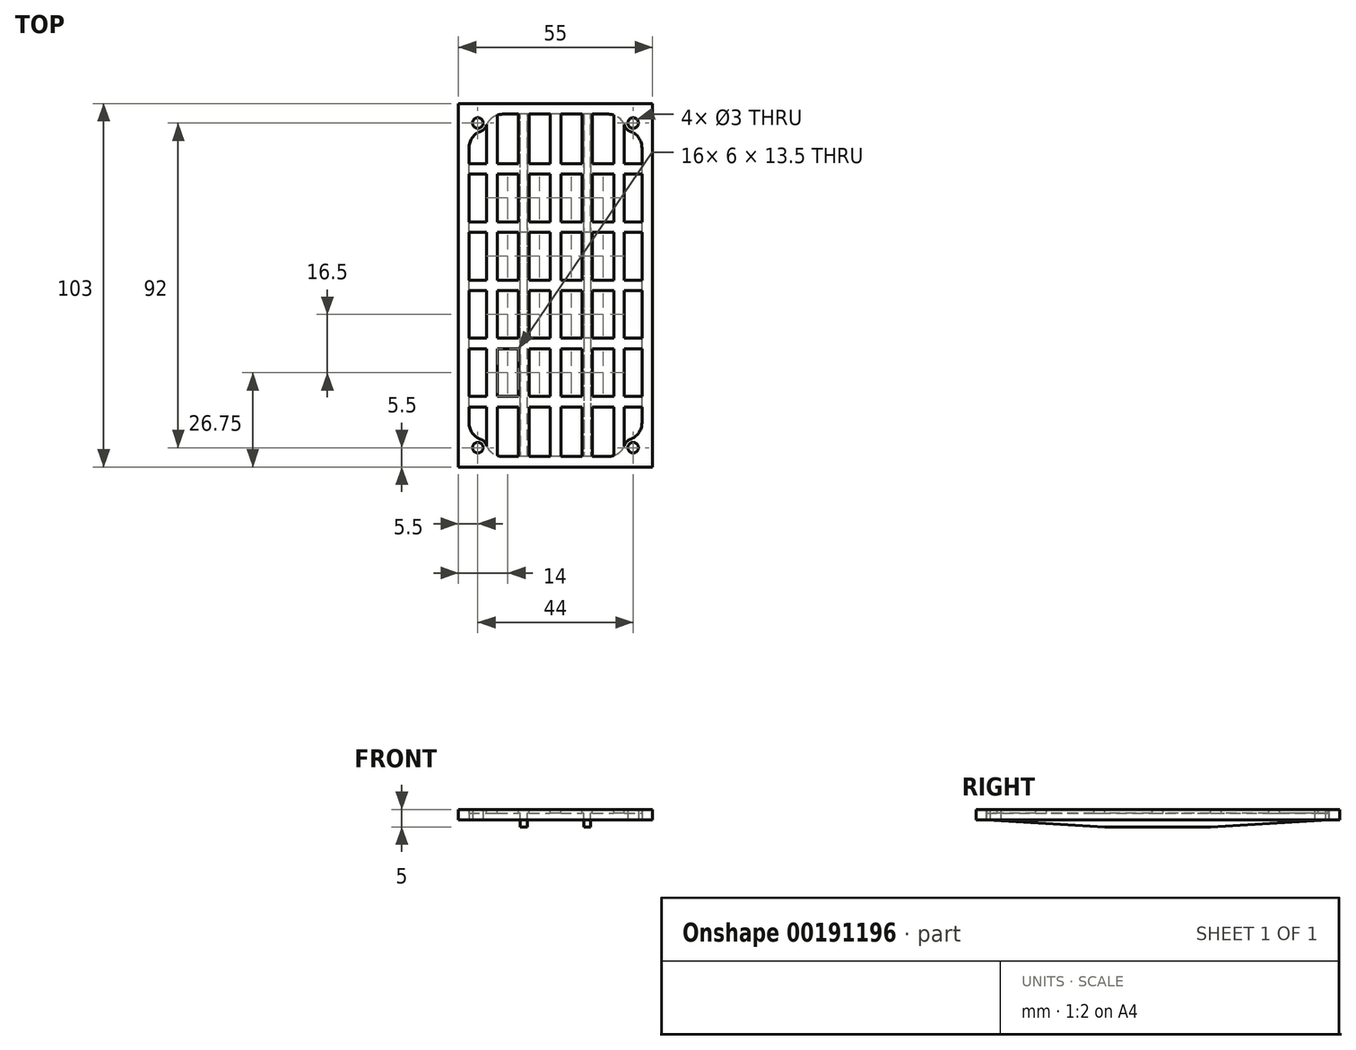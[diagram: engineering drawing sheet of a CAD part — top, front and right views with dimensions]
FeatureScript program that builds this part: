
annotation { "Feature Type Name" : "Feature", "Feature Type Description" : "" }
export const myFeature = defineFeature(function(context is Context, id is Id, definition is map)
    precondition{}
    {
        {
            var Q0;
            Q0=qCreatedBy(makeId("Top.planeOp"),FACE);
            var sketch = newSketch(context, id + "F0", { "sketchPlane" : qUnion([Q0])});
            skLineSegment(sketch, "E0.bottom", {"start": v(27.5, -51.5) * mm, "end": v(-27.5, -51.5) * mm});
            skLineSegment(sketch, "E0.top", {"start": v(27.5, 51.5) * mm, "end": v(-27.5, 51.5) * mm});
            skLineSegment(sketch, "E0.left", {"start": v(27.5, -51.5) * mm, "end": v(27.5, 51.5) * mm});
            skLineSegment(sketch, "E0.right", {"start": v(-27.5, -51.5) * mm, "end": v(-27.5, 51.5) * mm});
            skLineSegment(sketch, "E1.0", {"start": v(-27.5, -51.5) * mm, "end": v(-27.5, 48.5) * mm});
            skLineSegment(sketch, "E2.0", {"start": v(14.93, 48.5) * mm, "end": v(-14.93, 48.5) * mm});
            skLineSegment(sketch, "E3.0", {"start": v(14.93, -48.5) * mm, "end": v(-14.93, -48.5) * mm});
            skLineSegment(sketch, "E4.0", {"start": v(24.5, -38.93) * mm, "end": v(24.5, 38.93) * mm});
            skCircle(sketch, "E5", {"center": v(-22, 46) * mm, "radius": 1.5 * mm});
            skArc(sketch, "E6", {"start": v(-21.17, 43.64) * mm, "mid": v(-20.23, 44.23) * mm, "end": v(-19.64, 45.17) * mm});
            skCircle(sketch, "E7", {"center": v(22, 46) * mm, "radius": 1.5 * mm});
            skArc(sketch, "E8", {"start": v(19.64, 45.17) * mm, "mid": v(20.23, 44.23) * mm, "end": v(21.17, 43.64) * mm});
            skCircle(sketch, "E9", {"center": v(-22, -46) * mm, "radius": 1.5 * mm});
            skArc(sketch, "E10", {"start": v(-19.64, -45.17) * mm, "mid": v(-20.23, -44.23) * mm, "end": v(-21.17, -43.64) * mm});
            skCircle(sketch, "E11", {"center": v(22, -46) * mm, "radius": 1.5 * mm});
            skArc(sketch, "E12", {"start": v(21.17, -43.64) * mm, "mid": v(20.23, -44.23) * mm, "end": v(19.64, -45.17) * mm});
            skPoint(sketch, "E13.visualSharp", {"position": v(24.5, -46) * mm});
            skArc(sketch, "E13.filletArc", {"start": v(21.17, -43.64) * mm, "mid": v(23.58, -41.82) * mm, "end": v(24.5, -38.93) * mm});
            skPoint(sketch, "E14.visualSharp", {"position": v(22, -48.5) * mm});
            skArc(sketch, "E14.filletArc", {"start": v(14.93, -48.5) * mm, "mid": v(17.82, -47.58) * mm, "end": v(19.64, -45.17) * mm});
            skPoint(sketch, "E15.visualSharp", {"position": v(22, 48.5) * mm});
            skArc(sketch, "E15.filletArc", {"start": v(19.64, 45.17) * mm, "mid": v(17.82, 47.58) * mm, "end": v(14.93, 48.5) * mm});
            skPoint(sketch, "E16.visualSharp", {"position": v(24.5, 46) * mm});
            skArc(sketch, "E16.filletArc", {"start": v(24.5, 38.93) * mm, "mid": v(23.58, 41.82) * mm, "end": v(21.17, 43.64) * mm});
            skLineSegment(sketch, "E17", {"start": v(-24.5, -38.93) * mm, "end": v(-24.5, 38.93) * mm});
            skPoint(sketch, "E18.visualSharp", {"position": v(-24.5, -46) * mm});
            skArc(sketch, "E18.filletArc", {"start": v(-24.5, -38.93) * mm, "mid": v(-23.58, -41.82) * mm, "end": v(-21.17, -43.64) * mm});
            skPoint(sketch, "E19.visualSharp", {"position": v(-22, -48.5) * mm});
            skArc(sketch, "E19.filletArc", {"start": v(-19.64, -45.17) * mm, "mid": v(-17.82, -47.58) * mm, "end": v(-14.93, -48.5) * mm});
            skPoint(sketch, "E20.visualSharp", {"position": v(-24.5, 46) * mm});
            skArc(sketch, "E20.filletArc", {"start": v(-21.17, 43.64) * mm, "mid": v(-23.58, 41.82) * mm, "end": v(-24.5, 38.93) * mm});
            skPoint(sketch, "E21.visualSharp", {"position": v(-22, 48.5) * mm});
            skArc(sketch, "E21.filletArc", {"start": v(-14.93, 48.5) * mm, "mid": v(-17.82, 47.58) * mm, "end": v(-19.64, 45.17) * mm});
            skSolve(sketch);
        }
        {
            var Q0;
            Q0 = qSketchRegion(id + "F0", true);
            extrude(context, id + "F1", {"entities" : qUnion([Q0]), "depth" : 3 * mm});
        }
        {
            var Q0;
            Q0=makeQuery(id+"F1.opExtrude","CAP_FACE",FACE,{"disambiguationData":[OSD([sQuery(id+"F0.wireOp",EDGE,"E0.bottom"),sQuery(id+"F0.wireOp",EDGE,"E0.top"),sQuery(id+"F0.wireOp",EDGE,"E0.left"),sQuery(id+"F0.wireOp",EDGE,"E0.right"),sQuery(id+"F0.wireOp",EDGE,"E2.0"),sQuery(id+"F0.wireOp",EDGE,"E3.0"),sQuery(id+"F0.wireOp",EDGE,"E4.0"),sQuery(id+"F0.wireOp",EDGE,"E5"),sQuery(id+"F0.wireOp",EDGE,"E6"),sQuery(id+"F0.wireOp",EDGE,"E7"),sQuery(id+"F0.wireOp",EDGE,"E8"),sQuery(id+"F0.wireOp",EDGE,"E9"),sQuery(id+"F0.wireOp",EDGE,"E10"),sQuery(id+"F0.wireOp",EDGE,"E11"),sQuery(id+"F0.wireOp",EDGE,"E12"),sQuery(id+"F0.wireOp",EDGE,"E13.filletArc"),sQuery(id+"F0.wireOp",EDGE,"E14.filletArc"),sQuery(id+"F0.wireOp",EDGE,"E15.filletArc"),sQuery(id+"F0.wireOp",EDGE,"E16.filletArc"),sQuery(id+"F0.wireOp",EDGE,"E17"),sQuery(id+"F0.wireOp",EDGE,"E18.filletArc"),sQuery(id+"F0.wireOp",EDGE,"E19.filletArc"),sQuery(id+"F0.wireOp",EDGE,"E20.filletArc"),sQuery(id+"F0.wireOp",EDGE,"E21.filletArc")])],"isStart":false});
            var sketch = newSketch(context, id + "F2", { "sketchPlane" : qUnion([Q0])});
            skLineSegment(sketch, "E22.0", {"start": v(14.93, 48.5) * mm, "end": v(-14.93, 48.5) * mm});
            skLineSegment(sketch, "E22.1", {"start": v(14.93, -48.5) * mm, "end": v(-14.93, -48.5) * mm});
            skLineSegment(sketch, "E22.2", {"start": v(24.5, -38.93) * mm, "end": v(24.5, 38.93) * mm});
            skLineSegment(sketch, "E22.3", {"start": v(-24.5, -38.93) * mm, "end": v(-24.5, 38.93) * mm});
            skArc(sketch, "E22.4", {"start": v(-19.64, -45.17) * mm, "mid": v(-17.82, -47.58) * mm, "end": v(-14.93, -48.5) * mm});
            skArc(sketch, "E22.5", {"start": v(-24.5, -38.93) * mm, "mid": v(-23.58, -41.82) * mm, "end": v(-21.17, -43.64) * mm});
            skArc(sketch, "E22.6", {"start": v(-19.64, -45.17) * mm, "mid": v(-20.23, -44.23) * mm, "end": v(-21.17, -43.64) * mm});
            skArc(sketch, "E22.7", {"start": v(14.93, -48.5) * mm, "mid": v(17.82, -47.58) * mm, "end": v(19.64, -45.17) * mm});
            skArc(sketch, "E22.8", {"start": v(21.17, -43.64) * mm, "mid": v(23.58, -41.82) * mm, "end": v(24.5, -38.93) * mm});
            skArc(sketch, "E22.9", {"start": v(21.17, -43.64) * mm, "mid": v(20.23, -44.23) * mm, "end": v(19.64, -45.17) * mm});
            skArc(sketch, "E22.10", {"start": v(24.5, 38.93) * mm, "mid": v(23.58, 41.82) * mm, "end": v(21.17, 43.64) * mm});
            skArc(sketch, "E22.11", {"start": v(19.64, 45.17) * mm, "mid": v(20.23, 44.23) * mm, "end": v(21.17, 43.64) * mm});
            skArc(sketch, "E22.12", {"start": v(19.64, 45.17) * mm, "mid": v(17.82, 47.58) * mm, "end": v(14.93, 48.5) * mm});
            skArc(sketch, "E22.13", {"start": v(-21.17, 43.64) * mm, "mid": v(-23.58, 41.82) * mm, "end": v(-24.5, 38.93) * mm});
            skArc(sketch, "E22.14", {"start": v(-14.93, 48.5) * mm, "mid": v(-17.82, 47.58) * mm, "end": v(-19.64, 45.17) * mm});
            skArc(sketch, "E22.15", {"start": v(-21.17, 43.64) * mm, "mid": v(-20.23, 44.23) * mm, "end": v(-19.64, 45.17) * mm});
            skPoint(sketch, "E22.16", {"position": v(17.82, -47.58) * mm});
            skPoint(sketch, "E22.17", {"position": v(20.23, -44.23) * mm});
            skLineSegment(sketch, "E23.0", {"start": v(-1.5, 48.5) * mm, "end": v(-1.5, 34.5) * mm});
            skLineSegment(sketch, "E24.0", {"start": v(1.5, 48.5) * mm, "end": v(1.5, 34.5) * mm});
            skLineSegment(sketch, "E25.1.0.0", {"start": v(10.5, 48.5) * mm, "end": v(10.5, 34.5) * mm});
            skLineSegment(sketch, "E25.1.0.1", {"start": v(7.5, 48.5) * mm, "end": v(7.5, 34.5) * mm});
            skLineSegment(sketch, "E25.2.0.0", {"start": v(19.5, 45.53) * mm, "end": v(19.5, 34.5) * mm});
            skLineSegment(sketch, "E25.2.0.1", {"start": v(16.5, 48.25) * mm, "end": v(16.5, 34.5) * mm});
            skLineSegment(sketch, "E25.direction1", {"start": v(-1.5, -48.5) * mm, "end": v(7.5, -48.5) * mm, "construction": true});
            skLineSegment(sketch, "E26.MirrorCS", {"start": v(-7.5, 48.5) * mm, "end": v(-7.5, 34.5) * mm});
            skLineSegment(sketch, "E27.MirrorCS", {"start": v(-10.5, 48.5) * mm, "end": v(-10.5, 34.5) * mm});
            skLineSegment(sketch, "E28.MirrorCS", {"start": v(-19.5, 45.53) * mm, "end": v(-19.5, 34.5) * mm});
            skLineSegment(sketch, "E29.MirrorCS", {"start": v(-16.5, 48.25) * mm, "end": v(-16.5, 34.5) * mm});
            skLineSegment(sketch, "E30.0", {"start": v(-24.5, -1.5) * mm, "end": v(-19.5, -1.5) * mm});
            skLineSegment(sketch, "E31.0", {"start": v(-24.5, 1.5) * mm, "end": v(-19.5, 1.5) * mm});
            skLineSegment(sketch, "E32.0.1.0", {"start": v(-24.5, 18) * mm, "end": v(-19.5, 18) * mm});
            skLineSegment(sketch, "E32.0.1.1", {"start": v(-24.5, 15) * mm, "end": v(-19.5, 15) * mm});
            skLineSegment(sketch, "E32.direction1", {"start": v(-24.5, -1.5) * mm, "end": v(-19.5, -1.5) * mm, "construction": true});
            skLineSegment(sketch, "E32.direction2", {"start": v(-24.5, -1.5) * mm, "end": v(-24.5, 15) * mm, "construction": true});
            skLineSegment(sketch, "E33.0.0.2", {"start": v(-24.5, 34.5) * mm, "end": v(-19.5, 34.5) * mm});
            skLineSegment(sketch, "E33.3.0.2", {"start": v(-24.5, 31.5) * mm, "end": v(-19.5, 31.5) * mm});
            skLineSegment(sketch, "E34.MirrorCS", {"start": v(-24.5, -18) * mm, "end": v(-19.5, -18) * mm});
            skLineSegment(sketch, "E35.MirrorCS", {"start": v(-24.5, -31.5) * mm, "end": v(-19.5, -31.5) * mm});
            skLineSegment(sketch, "E36.MirrorCS", {"start": v(-24.5, -15) * mm, "end": v(-19.5, -15) * mm});
            skLineSegment(sketch, "E37.MirrorCS", {"start": v(-24.5, -34.5) * mm, "end": v(-19.5, -34.5) * mm});
            skPoint(sketch, "E38.orphan", {"position": v(-19.5, 48.5) * mm});
            skPoint(sketch, "E39.orphan", {"position": v(-16.5, 48.5) * mm});
            skLineSegment(sketch, "E40.trimOffspring", {"start": v(-16.5, 34.5) * mm, "end": v(-10.5, 34.5) * mm});
            skLineSegment(sketch, "E41.trimOffspring", {"start": v(-16.5, 31.5) * mm, "end": v(-10.5, 31.5) * mm});
            skLineSegment(sketch, "E42.trimOffspring", {"start": v(-16.5, 31.5) * mm, "end": v(-16.5, 18) * mm});
            skLineSegment(sketch, "E43.trimOffspring", {"start": v(-19.5, 31.5) * mm, "end": v(-19.5, 18) * mm});
            skLineSegment(sketch, "E44.trimOffspring", {"start": v(-10.5, 31.5) * mm, "end": v(-10.5, 18) * mm});
            skLineSegment(sketch, "E45.trimOffspring", {"start": v(-7.5, 31.5) * mm, "end": v(-7.5, 18) * mm});
            skLineSegment(sketch, "E46.trimOffspring", {"start": v(-7.5, 34.5) * mm, "end": v(-1.5, 34.5) * mm});
            skLineSegment(sketch, "E47.trimOffspring", {"start": v(-7.5, 31.5) * mm, "end": v(-1.5, 31.5) * mm});
            skLineSegment(sketch, "E48.trimOffspring", {"start": v(1.5, 31.5) * mm, "end": v(7.5, 31.5) * mm});
            skLineSegment(sketch, "E49.trimOffspring", {"start": v(1.5, 34.5) * mm, "end": v(7.5, 34.5) * mm});
            skLineSegment(sketch, "E50.trimOffspring", {"start": v(1.5, 31.5) * mm, "end": v(1.5, 18) * mm});
            skLineSegment(sketch, "E51.trimOffspring", {"start": v(-1.5, 31.5) * mm, "end": v(-1.5, 18) * mm});
            skLineSegment(sketch, "E52.trimOffspring", {"start": v(7.5, 31.5) * mm, "end": v(7.5, 18) * mm});
            skLineSegment(sketch, "E53.trimOffspring", {"start": v(10.5, 31.5) * mm, "end": v(10.5, 18) * mm});
            skLineSegment(sketch, "E54.trimOffspring", {"start": v(10.5, 34.5) * mm, "end": v(16.5, 34.5) * mm});
            skLineSegment(sketch, "E55.trimOffspring", {"start": v(10.5, 31.5) * mm, "end": v(16.5, 31.5) * mm});
            skLineSegment(sketch, "E56.trimOffspring", {"start": v(19.5, 34.5) * mm, "end": v(24.5, 34.5) * mm});
            skLineSegment(sketch, "E57.trimOffspring", {"start": v(19.5, 31.5) * mm, "end": v(24.5, 31.5) * mm});
            skLineSegment(sketch, "E58.trimOffspring", {"start": v(19.5, 31.5) * mm, "end": v(19.5, 18) * mm});
            skLineSegment(sketch, "E59.trimOffspring", {"start": v(16.5, 31.5) * mm, "end": v(16.5, 18) * mm});
            skPoint(sketch, "E60.orphan", {"position": v(19.5, 48.5) * mm});
            skPoint(sketch, "E61.orphan", {"position": v(16.5, 48.5) * mm});
            skLineSegment(sketch, "E62.trimOffspring", {"start": v(-16.5, 18) * mm, "end": v(-10.5, 18) * mm});
            skLineSegment(sketch, "E63.trimOffspring", {"start": v(-7.5, 18) * mm, "end": v(-1.5, 18) * mm});
            skLineSegment(sketch, "E64.trimOffspring", {"start": v(1.5, 18) * mm, "end": v(7.5, 18) * mm});
            skLineSegment(sketch, "E65.trimOffspring", {"start": v(10.5, 18) * mm, "end": v(16.5, 18) * mm});
            skLineSegment(sketch, "E66.trimOffspring", {"start": v(19.5, 18) * mm, "end": v(24.5, 18) * mm});
            skLineSegment(sketch, "E67.trimOffspring", {"start": v(19.5, 15) * mm, "end": v(24.5, 15) * mm});
            skLineSegment(sketch, "E68.trimOffspring", {"start": v(19.5, 15) * mm, "end": v(19.5, 1.5) * mm});
            skLineSegment(sketch, "E69.trimOffspring", {"start": v(16.5, 15) * mm, "end": v(16.5, 1.5) * mm});
            skLineSegment(sketch, "E70.trimOffspring", {"start": v(10.5, 15) * mm, "end": v(10.5, 1.5) * mm});
            skLineSegment(sketch, "E71.trimOffspring", {"start": v(7.5, 15) * mm, "end": v(7.5, 1.5) * mm});
            skLineSegment(sketch, "E72.trimOffspring", {"start": v(1.5, 15) * mm, "end": v(1.5, 1.5) * mm});
            skLineSegment(sketch, "E73.trimOffspring", {"start": v(-1.5, 15) * mm, "end": v(-1.5, 1.5) * mm});
            skLineSegment(sketch, "E74.trimOffspring", {"start": v(-7.5, 15) * mm, "end": v(-7.5, 1.5) * mm});
            skLineSegment(sketch, "E75.trimOffspring", {"start": v(-10.5, 15) * mm, "end": v(-10.5, 1.5) * mm});
            skLineSegment(sketch, "E76.trimOffspring", {"start": v(-16.5, 15) * mm, "end": v(-16.5, 1.5) * mm});
            skLineSegment(sketch, "E77.trimOffspring", {"start": v(-19.5, 15) * mm, "end": v(-19.5, 1.5) * mm});
            skLineSegment(sketch, "E78.trimOffspring", {"start": v(-16.5, 15) * mm, "end": v(-10.5, 15) * mm});
            skLineSegment(sketch, "E79.trimOffspring", {"start": v(-7.5, 15) * mm, "end": v(-1.5, 15) * mm});
            skLineSegment(sketch, "E80.trimOffspring", {"start": v(1.5, 15) * mm, "end": v(7.5, 15) * mm});
            skLineSegment(sketch, "E81.trimOffspring", {"start": v(10.5, 15) * mm, "end": v(16.5, 15) * mm});
            skLineSegment(sketch, "E82.trimOffspring", {"start": v(-16.5, 1.5) * mm, "end": v(-10.5, 1.5) * mm});
            skLineSegment(sketch, "E83.trimOffspring", {"start": v(-16.5, -1.5) * mm, "end": v(-10.5, -1.5) * mm, "construction": true});
            skLineSegment(sketch, "E84.trimOffspring", {"start": v(-16.5, -1.5) * mm, "end": v(-16.5, -15) * mm});
            skLineSegment(sketch, "E85.trimOffspring", {"start": v(19.5, 1.5) * mm, "end": v(24.5, 1.5) * mm});
            skLineSegment(sketch, "E86.trimOffspring", {"start": v(19.5, -1.5) * mm, "end": v(24.5, -1.5) * mm});
            skLineSegment(sketch, "E87.trimOffspring", {"start": v(19.5, -1.5) * mm, "end": v(19.5, -15) * mm});
            skLineSegment(sketch, "E88.trimOffspring", {"start": v(16.5, -1.5) * mm, "end": v(16.5, -15) * mm});
            skLineSegment(sketch, "E89.trimOffspring", {"start": v(10.5, -1.5) * mm, "end": v(10.5, -15) * mm});
            skLineSegment(sketch, "E90.trimOffspring", {"start": v(7.5, -1.5) * mm, "end": v(7.5, -15) * mm});
            skLineSegment(sketch, "E91.trimOffspring", {"start": v(1.5, -1.5) * mm, "end": v(1.5, -15) * mm});
            skLineSegment(sketch, "E92.trimOffspring", {"start": v(-1.5, -1.5) * mm, "end": v(-1.5, -15) * mm});
            skLineSegment(sketch, "E93.trimOffspring", {"start": v(1.5, 1.5) * mm, "end": v(7.5, 1.5) * mm});
            skLineSegment(sketch, "E94.trimOffspring", {"start": v(10.5, -1.5) * mm, "end": v(16.5, -1.5) * mm});
            skLineSegment(sketch, "E95.trimOffspring", {"start": v(10.5, 1.5) * mm, "end": v(16.5, 1.5) * mm});
            skLineSegment(sketch, "E96.trimOffspring", {"start": v(1.5, -1.5) * mm, "end": v(7.5, -1.5) * mm});
            skLineSegment(sketch, "E97.trimOffspring", {"start": v(-7.5, -1.5) * mm, "end": v(-1.5, -1.5) * mm, "construction": true});
            skLineSegment(sketch, "E98.trimOffspring", {"start": v(-7.5, 1.5) * mm, "end": v(-1.5, 1.5) * mm});
            skLineSegment(sketch, "E99.trimOffspring", {"start": v(-7.5, -1.5) * mm, "end": v(-7.5, -15) * mm});
            skLineSegment(sketch, "E100.trimOffspring", {"start": v(-10.5, -1.5) * mm, "end": v(-10.5, -15) * mm});
            skLineSegment(sketch, "E101.trimOffspring", {"start": v(-19.5, -1.5) * mm, "end": v(-19.5, -15) * mm});
            skLineSegment(sketch, "E102.trimOffspring", {"start": v(-16.5, -1.5) * mm, "end": v(-10.5, -1.5) * mm});
            skLineSegment(sketch, "E103.trimOffspring", {"start": v(-7.5, -1.5) * mm, "end": v(-1.5, -1.5) * mm});
            skLineSegment(sketch, "E104.trimOffspring", {"start": v(-16.5, -15) * mm, "end": v(-10.5, -15) * mm});
            skLineSegment(sketch, "E105.trimOffspring", {"start": v(-16.5, -18) * mm, "end": v(-10.5, -18) * mm});
            skLineSegment(sketch, "E106.trimOffspring", {"start": v(-16.5, -18) * mm, "end": v(-16.5, -31.5) * mm});
            skLineSegment(sketch, "E107.trimOffspring", {"start": v(-19.5, -18) * mm, "end": v(-19.5, -31.5) * mm});
            skLineSegment(sketch, "E108.trimOffspring", {"start": v(-10.5, -18) * mm, "end": v(-10.5, -31.5) * mm});
            skLineSegment(sketch, "E109.trimOffspring", {"start": v(-7.5, -18) * mm, "end": v(-7.5, -31.5) * mm});
            skLineSegment(sketch, "E110.trimOffspring", {"start": v(-7.5, -15) * mm, "end": v(-1.5, -15) * mm});
            skLineSegment(sketch, "E111.trimOffspring", {"start": v(-7.5, -18) * mm, "end": v(-1.5, -18) * mm});
            skLineSegment(sketch, "E112.trimOffspring", {"start": v(1.5, -18) * mm, "end": v(7.5, -18) * mm});
            skLineSegment(sketch, "E113.trimOffspring", {"start": v(1.5, -18) * mm, "end": v(1.5, -31.5) * mm});
            skLineSegment(sketch, "E114.trimOffspring", {"start": v(-1.5, -18) * mm, "end": v(-1.5, -31.5) * mm});
            skLineSegment(sketch, "E115.trimOffspring", {"start": v(7.5, -18) * mm, "end": v(7.5, -31.5) * mm});
            skLineSegment(sketch, "E116.trimOffspring", {"start": v(10.5, -18) * mm, "end": v(10.5, -31.5) * mm});
            skLineSegment(sketch, "E117.trimOffspring", {"start": v(10.5, -15) * mm, "end": v(16.5, -15) * mm});
            skLineSegment(sketch, "E118.trimOffspring", {"start": v(10.5, -18) * mm, "end": v(16.5, -18) * mm});
            skLineSegment(sketch, "E119.trimOffspring", {"start": v(1.5, -15) * mm, "end": v(7.5, -15) * mm});
            skLineSegment(sketch, "E120.trimOffspring", {"start": v(19.5, -15) * mm, "end": v(24.5, -15) * mm});
            skLineSegment(sketch, "E121.trimOffspring", {"start": v(19.5, -18) * mm, "end": v(24.5, -18) * mm});
            skLineSegment(sketch, "E122.trimOffspring", {"start": v(19.5, -18) * mm, "end": v(19.5, -31.5) * mm});
            skLineSegment(sketch, "E123.trimOffspring", {"start": v(16.5, -18) * mm, "end": v(16.5, -31.5) * mm});
            skLineSegment(sketch, "E124.trimOffspring", {"start": v(-16.5, -31.5) * mm, "end": v(-10.5, -31.5) * mm});
            skLineSegment(sketch, "E125.trimOffspring", {"start": v(-16.5, -34.5) * mm, "end": v(-10.5, -34.5) * mm});
            skLineSegment(sketch, "E126.trimOffspring", {"start": v(-16.5, -34.5) * mm, "end": v(-16.5, -48.25) * mm});
            skLineSegment(sketch, "E127.trimOffspring", {"start": v(-19.5, -34.5) * mm, "end": v(-19.5, -45.53) * mm});
            skLineSegment(sketch, "E128.trimOffspring", {"start": v(-10.5, -34.5) * mm, "end": v(-10.5, -48.5) * mm});
            skLineSegment(sketch, "E129.trimOffspring", {"start": v(-7.5, -34.5) * mm, "end": v(-7.5, -48.5) * mm});
            skLineSegment(sketch, "E130.trimOffspring", {"start": v(1.5, -34.5) * mm, "end": v(7.5, -34.5) * mm});
            skLineSegment(sketch, "E131.trimOffspring", {"start": v(1.5, -31.5) * mm, "end": v(7.5, -31.5) * mm});
            skLineSegment(sketch, "E132.trimOffspring", {"start": v(10.5, -34.5) * mm, "end": v(16.5, -34.5) * mm});
            skLineSegment(sketch, "E133.trimOffspring", {"start": v(19.5, -31.5) * mm, "end": v(24.5, -31.5) * mm});
            skLineSegment(sketch, "E134.trimOffspring", {"start": v(19.5, -34.5) * mm, "end": v(24.5, -34.5) * mm});
            skLineSegment(sketch, "E135.trimOffspring", {"start": v(19.5, -34.5) * mm, "end": v(19.5, -45.53) * mm});
            skLineSegment(sketch, "E136.trimOffspring", {"start": v(16.5, -34.5) * mm, "end": v(16.5, -48.25) * mm});
            skLineSegment(sketch, "E137.trimOffspring", {"start": v(10.5, -34.5) * mm, "end": v(10.5, -48.5) * mm});
            skLineSegment(sketch, "E138.trimOffspring", {"start": v(10.5, -31.5) * mm, "end": v(16.5, -31.5) * mm});
            skLineSegment(sketch, "E139.trimOffspring", {"start": v(7.5, -34.5) * mm, "end": v(7.5, -48.5) * mm});
            skLineSegment(sketch, "E140.trimOffspring", {"start": v(1.5, -34.5) * mm, "end": v(1.5, -48.5) * mm});
            skLineSegment(sketch, "E141", {"start": v(-7.5, -31.5) * mm, "end": v(-1.5, -31.5) * mm});
            skLineSegment(sketch, "E142", {"start": v(-7.5, -34.5) * mm, "end": v(-1.5, -34.5) * mm});
            skLineSegment(sketch, "E143.trimOffspring", {"start": v(-1.5, -34.5) * mm, "end": v(-1.5, -48.5) * mm});
            skPoint(sketch, "E144.orphan", {"position": v(19.5, -48.5) * mm});
            skPoint(sketch, "E145.orphan", {"position": v(16.5, -48.5) * mm});
            skPoint(sketch, "E146.orphan", {"position": v(-16.5, -48.5) * mm});
            skPoint(sketch, "E147.orphan", {"position": v(-19.5, -48.5) * mm});
            skSolve(sketch);
        }
        {
            var Q0;
            {var subQ19=sQuery(id+"F2.wireOp",EDGE,"E23.0");Q0=makeQuery(id+"F2.imprint","IMPRINT",FACE,{"disambiguationData":[TD([[makeQuery(id+"F2.imprint","IMPRINT",EDGE,{"derivedFrom":subQ19}),1.0]])]});}
            extrude(context, id + "F3", {"entities" : qUnion([Q0]), "operationType" : NewBodyOperationType.ADD, "oppositeDirection" : true, "depth" : 1 * mm});
        }
        {
            var Q0;
            Q0=makeQuery(id+"F3.opExtrude","CAP_FACE",FACE,{"disambiguationData":[OSD([sQuery(id+"F2.wireOp",EDGE,"E22.0"),sQuery(id+"F2.wireOp",EDGE,"E22.1"),sQuery(id+"F2.wireOp",EDGE,"E22.2"),sQuery(id+"F2.wireOp",EDGE,"E22.3"),sQuery(id+"F2.wireOp",EDGE,"E22.4"),sQuery(id+"F2.wireOp",EDGE,"E22.7"),sQuery(id+"F2.wireOp",EDGE,"E22.12"),sQuery(id+"F2.wireOp",EDGE,"E22.14"),sQuery(id+"F2.wireOp",EDGE,"E23.0"),sQuery(id+"F2.wireOp",EDGE,"E24.0"),sQuery(id+"F2.wireOp",EDGE,"E25.1.0.0"),sQuery(id+"F2.wireOp",EDGE,"E25.1.0.1"),sQuery(id+"F2.wireOp",EDGE,"E25.2.0.0"),sQuery(id+"F2.wireOp",EDGE,"E25.2.0.1"),sQuery(id+"F2.wireOp",EDGE,"E26.MirrorCS"),sQuery(id+"F2.wireOp",EDGE,"E27.MirrorCS"),sQuery(id+"F2.wireOp",EDGE,"E28.MirrorCS"),sQuery(id+"F2.wireOp",EDGE,"E29.MirrorCS"),sQuery(id+"F2.wireOp",EDGE,"E30.0"),sQuery(id+"F2.wireOp",EDGE,"E31.0"),sQuery(id+"F2.wireOp",EDGE,"E32.0.1.0"),sQuery(id+"F2.wireOp",EDGE,"E32.0.1.1"),sQuery(id+"F2.wireOp",EDGE,"E33.0.0.2"),sQuery(id+"F2.wireOp",EDGE,"E33.3.0.2"),sQuery(id+"F2.wireOp",EDGE,"E34.MirrorCS"),sQuery(id+"F2.wireOp",EDGE,"E35.MirrorCS"),sQuery(id+"F2.wireOp",EDGE,"E36.MirrorCS"),sQuery(id+"F2.wireOp",EDGE,"E37.MirrorCS"),sQuery(id+"F2.wireOp",EDGE,"E40.trimOffspring"),sQuery(id+"F2.wireOp",EDGE,"E41.trimOffspring"),sQuery(id+"F2.wireOp",EDGE,"E42.trimOffspring"),sQuery(id+"F2.wireOp",EDGE,"E43.trimOffspring"),sQuery(id+"F2.wireOp",EDGE,"E44.trimOffspring"),sQuery(id+"F2.wireOp",EDGE,"E45.trimOffspring"),sQuery(id+"F2.wireOp",EDGE,"E46.trimOffspring"),sQuery(id+"F2.wireOp",EDGE,"E47.trimOffspring"),sQuery(id+"F2.wireOp",EDGE,"E48.trimOffspring"),sQuery(id+"F2.wireOp",EDGE,"E49.trimOffspring"),sQuery(id+"F2.wireOp",EDGE,"E50.trimOffspring"),sQuery(id+"F2.wireOp",EDGE,"E51.trimOffspring"),sQuery(id+"F2.wireOp",EDGE,"E52.trimOffspring"),sQuery(id+"F2.wireOp",EDGE,"E53.trimOffspring"),sQuery(id+"F2.wireOp",EDGE,"E54.trimOffspring"),sQuery(id+"F2.wireOp",EDGE,"E55.trimOffspring"),sQuery(id+"F2.wireOp",EDGE,"E56.trimOffspring"),sQuery(id+"F2.wireOp",EDGE,"E57.trimOffspring"),sQuery(id+"F2.wireOp",EDGE,"E58.trimOffspring"),sQuery(id+"F2.wireOp",EDGE,"E59.trimOffspring"),sQuery(id+"F2.wireOp",EDGE,"E62.trimOffspring"),sQuery(id+"F2.wireOp",EDGE,"E63.trimOffspring"),sQuery(id+"F2.wireOp",EDGE,"E64.trimOffspring"),sQuery(id+"F2.wireOp",EDGE,"E65.trimOffspring"),sQuery(id+"F2.wireOp",EDGE,"E66.trimOffspring"),sQuery(id+"F2.wireOp",EDGE,"E67.trimOffspring"),sQuery(id+"F2.wireOp",EDGE,"E68.trimOffspring"),sQuery(id+"F2.wireOp",EDGE,"E69.trimOffspring"),sQuery(id+"F2.wireOp",EDGE,"E70.trimOffspring"),sQuery(id+"F2.wireOp",EDGE,"E71.trimOffspring"),sQuery(id+"F2.wireOp",EDGE,"E72.trimOffspring"),sQuery(id+"F2.wireOp",EDGE,"E73.trimOffspring"),sQuery(id+"F2.wireOp",EDGE,"E74.trimOffspring"),sQuery(id+"F2.wireOp",EDGE,"E75.trimOffspring"),sQuery(id+"F2.wireOp",EDGE,"E76.trimOffspring"),sQuery(id+"F2.wireOp",EDGE,"E77.trimOffspring"),sQuery(id+"F2.wireOp",EDGE,"E78.trimOffspring"),sQuery(id+"F2.wireOp",EDGE,"E79.trimOffspring"),sQuery(id+"F2.wireOp",EDGE,"E80.trimOffspring"),sQuery(id+"F2.wireOp",EDGE,"E81.trimOffspring"),sQuery(id+"F2.wireOp",EDGE,"E82.trimOffspring"),sQuery(id+"F2.wireOp",EDGE,"E84.trimOffspring"),sQuery(id+"F2.wireOp",EDGE,"E85.trimOffspring"),sQuery(id+"F2.wireOp",EDGE,"E86.trimOffspring"),sQuery(id+"F2.wireOp",EDGE,"E87.trimOffspring"),sQuery(id+"F2.wireOp",EDGE,"E88.trimOffspring"),sQuery(id+"F2.wireOp",EDGE,"E89.trimOffspring"),sQuery(id+"F2.wireOp",EDGE,"E90.trimOffspring"),sQuery(id+"F2.wireOp",EDGE,"E91.trimOffspring"),sQuery(id+"F2.wireOp",EDGE,"E92.trimOffspring"),sQuery(id+"F2.wireOp",EDGE,"E93.trimOffspring"),sQuery(id+"F2.wireOp",EDGE,"E94.trimOffspring"),sQuery(id+"F2.wireOp",EDGE,"E95.trimOffspring"),sQuery(id+"F2.wireOp",EDGE,"E96.trimOffspring"),sQuery(id+"F2.wireOp",EDGE,"E98.trimOffspring"),sQuery(id+"F2.wireOp",EDGE,"E99.trimOffspring"),sQuery(id+"F2.wireOp",EDGE,"E100.trimOffspring"),sQuery(id+"F2.wireOp",EDGE,"E101.trimOffspring"),sQuery(id+"F2.wireOp",EDGE,"E102.trimOffspring"),sQuery(id+"F2.wireOp",EDGE,"E103.trimOffspring"),sQuery(id+"F2.wireOp",EDGE,"E104.trimOffspring"),sQuery(id+"F2.wireOp",EDGE,"E105.trimOffspring"),sQuery(id+"F2.wireOp",EDGE,"E106.trimOffspring"),sQuery(id+"F2.wireOp",EDGE,"E107.trimOffspring"),sQuery(id+"F2.wireOp",EDGE,"E108.trimOffspring"),sQuery(id+"F2.wireOp",EDGE,"E109.trimOffspring"),sQuery(id+"F2.wireOp",EDGE,"E110.trimOffspring"),sQuery(id+"F2.wireOp",EDGE,"E111.trimOffspring"),sQuery(id+"F2.wireOp",EDGE,"E112.trimOffspring"),sQuery(id+"F2.wireOp",EDGE,"E113.trimOffspring"),sQuery(id+"F2.wireOp",EDGE,"E114.trimOffspring"),sQuery(id+"F2.wireOp",EDGE,"E115.trimOffspring"),sQuery(id+"F2.wireOp",EDGE,"E116.trimOffspring"),sQuery(id+"F2.wireOp",EDGE,"E117.trimOffspring"),sQuery(id+"F2.wireOp",EDGE,"E118.trimOffspring"),sQuery(id+"F2.wireOp",EDGE,"E119.trimOffspring"),sQuery(id+"F2.wireOp",EDGE,"E120.trimOffspring"),sQuery(id+"F2.wireOp",EDGE,"E121.trimOffspring"),sQuery(id+"F2.wireOp",EDGE,"E122.trimOffspring"),sQuery(id+"F2.wireOp",EDGE,"E123.trimOffspring"),sQuery(id+"F2.wireOp",EDGE,"E124.trimOffspring"),sQuery(id+"F2.wireOp",EDGE,"E125.trimOffspring"),sQuery(id+"F2.wireOp",EDGE,"E126.trimOffspring"),sQuery(id+"F2.wireOp",EDGE,"E127.trimOffspring"),sQuery(id+"F2.wireOp",EDGE,"E128.trimOffspring"),sQuery(id+"F2.wireOp",EDGE,"E129.trimOffspring"),sQuery(id+"F2.wireOp",EDGE,"E130.trimOffspring"),sQuery(id+"F2.wireOp",EDGE,"E131.trimOffspring"),sQuery(id+"F2.wireOp",EDGE,"E132.trimOffspring"),sQuery(id+"F2.wireOp",EDGE,"E133.trimOffspring"),sQuery(id+"F2.wireOp",EDGE,"E134.trimOffspring"),sQuery(id+"F2.wireOp",EDGE,"E135.trimOffspring"),sQuery(id+"F2.wireOp",EDGE,"E136.trimOffspring"),sQuery(id+"F2.wireOp",EDGE,"E137.trimOffspring"),sQuery(id+"F2.wireOp",EDGE,"E138.trimOffspring"),sQuery(id+"F2.wireOp",EDGE,"E139.trimOffspring"),sQuery(id+"F2.wireOp",EDGE,"E140.trimOffspring"),sQuery(id+"F2.wireOp",EDGE,"E141"),sQuery(id+"F2.wireOp",EDGE,"E142"),sQuery(id+"F2.wireOp",EDGE,"E143.trimOffspring")])],"isStart":false});
            var sketch = newSketch(context, id + "F4", { "sketchPlane" : qUnion([Q0])});
            skLineSegment(sketch, "E148.0", {"start": v(-10, 48.5) * mm, "end": v(-10, -48.5) * mm});
            skLineSegment(sketch, "E149.0", {"start": v(-8, 48.5) * mm, "end": v(-8, -48.5) * mm});
            skLineSegment(sketch, "E150.0", {"start": v(10, -48.5) * mm, "end": v(10, 48.5) * mm});
            skLineSegment(sketch, "E151.0", {"start": v(8, -48.5) * mm, "end": v(8, 48.5) * mm});
            skLineSegment(sketch, "E152", {"start": v(-10, 48.5) * mm, "end": v(-8, 48.5) * mm});
            skLineSegment(sketch, "E153", {"start": v(8, 48.5) * mm, "end": v(10.5, 48.5) * mm});
            skLineSegment(sketch, "E154", {"start": v(-10, -48.5) * mm, "end": v(-8, -48.5) * mm});
            skLineSegment(sketch, "E155", {"start": v(8, -48.5) * mm, "end": v(10, -48.5) * mm});
            skSolve(sketch);
        }
        {
            var Q0;
            Q0 = qSketchRegion(id + "F4", true);
            extrude(context, id + "F5", {"entities" : qUnion([Q0]), "operationType" : NewBodyOperationType.ADD, "depth" : 4 * mm});
        }
        {
            var Q0;
            Q0=makeQuery(id+"F5.opExtrude","SWEPT_FACE",FACE,{"disambiguationData":[OSD([sQuery(id+"F4.wireOp",EDGE,"E148.0")])]});
            var sketch = newSketch(context, id + "F6", { "sketchPlane" : qUnion([Q0])});
            skLineSegment(sketch, "E156", {"start": v(0, -2) * mm, "end": v(15, -2) * mm});
            skLineSegment(sketch, "E157", {"start": v(15, -2) * mm, "end": v(-15, -2) * mm});
            skLineSegment(sketch, "E158", {"start": v(-15, -2) * mm, "end": v(-48.5, 0) * mm});
            skLineSegment(sketch, "E159", {"start": v(-48.5, 0) * mm, "end": v(-48.5, -2) * mm});
            skLineSegment(sketch, "E160", {"start": v(-48.5, -2) * mm, "end": v(-15, -2) * mm});
            skLineSegment(sketch, "E161", {"start": v(15, -2) * mm, "end": v(48.5, 0) * mm});
            skLineSegment(sketch, "E162", {"start": v(48.5, 0) * mm, "end": v(48.5, -2) * mm});
            skLineSegment(sketch, "E163", {"start": v(48.5, -2) * mm, "end": v(15, -2) * mm});
            skSolve(sketch);
        }
        {
            var Q0;
            Q0 = qSketchRegion(id + "F6", true);
            extrude(context, id + "F7", {"entities" : qUnion([Q0]), "operationType" : NewBodyOperationType.REMOVE, "oppositeDirection" : true, "depth" : 100 * mm});
        }
    });
